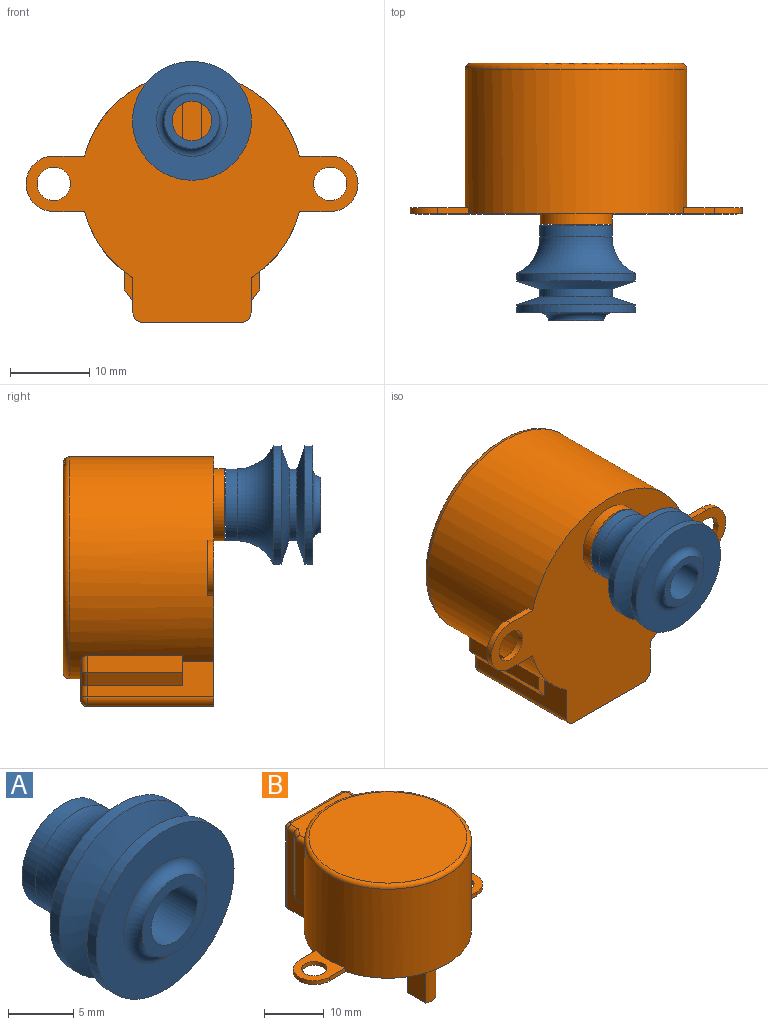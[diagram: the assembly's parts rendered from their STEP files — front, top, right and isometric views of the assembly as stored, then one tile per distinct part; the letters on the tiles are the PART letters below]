
ASSEMBLY  parts=2 mates=1
PART A: 12 faces, bbox 20.7x14.8x20.7 mm
  f0: cylinder r=7.5mm len=15mm, axis (0,-1,0), area 47.1mm2, adj f1,f10
  f1: cone r=4.55mm half-angle=71.3deg, axis (0,1,0), area 117.9mm2, adj f0,f2
  f2: cylinder r=4.55mm len=9.1mm, axis (0,-1,0), area 28.6mm2, adj f1,f3
  f3: cone r=4.55mm half-angle=71.3deg, axis (0,-1,0), area 117.9mm2, adj f2,f4
  f4: cylinder r=7.5mm len=15mm, axis (0,-1,0), area 47.1mm2, adj f3,f5
  f5: plane 15x15mm, normal (0,-1,0), area 113.2mm2, adj f4,f11
  f6: plane 6.99x6.99mm, normal (0,-1,0), area 18.8mm2, adj f7,f11
  f7: cylinder r=2.5mm len=12mm, axis (0,-1,0), area 188.3mm2, adj f6,f8
  f8: plane 9.1x9.1mm, normal (0,1,0), area 45.5mm2, adj f7,f9
  f9: cylinder r=4.55mm len=9.1mm, axis (0,-1,0), area 41.2mm2, adj f8,f10
  f10: torus R=9.55mm, axis (0,-1,0), area 201.3mm2, adj f0,f9
  f11: torus R=4.5mm, axis (0,1,0), area 38.1mm2, adj f5,f6
PART B: 43 faces, bbox 41.9x32.7x28.3 mm
  f0: plane 4.33x1.25mm, normal (0,0,-1), area 3.8mm2, adj f1,f4
  f1: cylinder r=2.5mm len=8mm, axis (0,0,1), area 62.8mm2, adj f0,f2,f3,f4,f5,f42
  f2: plane 4.33x1.25mm, normal (0,0,-1), area 3.8mm2, adj f1,f3
  f3: plane 6x4.33mm, normal (1,0,0), area 26mm2, adj f1,f2,f5
  f4: plane 6x4.33mm, normal (-1,0,0), area 26mm2, adj f0,f1,f5
  f5: plane 5x2.5mm, normal (0,0,-1), area 12mm2, adj f1,f3,f4
  f6: plane 16x4.45mm, normal (1,0,0), area 34.6mm2, adj f10,f12,f14,f15,f27,f28
  f7: plane 16x12.5mm, normal (0,1,0), area 200mm2, adj f10,f11,f12,f25
  f8: plane 16x4.45mm, normal (-1,0,0), area 34.6mm2, adj f10,f11,f16,f18,f23,f28
  f9: plane 15.54x5.05mm, normal (0,0,1), area 47.2mm2, adj f19,f20,f21,f22,f23,f24,f25,f26
  f10: plane 41.9x31.5mm, normal (0,0,-1), area 673.7mm2, adj f6,f7,f8,f11,f12,f28,f31,f32
  f11: cylinder r=1.2mm len=16mm, axis (0,0,-1), area 30.2mm2, adj f7,f8,f10,f24
  f12: cylinder r=1.2mm len=16mm, axis (0,0,-1), area 30.2mm2, adj f6,f7,f10,f26
  f13: plane 12x2.2mm, normal (1,0,0), area 26.4mm2, adj f14,f15,f20,f28
  f14: plane 12x1.63mm, normal (0.82,0.57,0), area 23.7mm2, adj f6,f13,f15,f19
  f15: plane 3.83x1.12mm, normal (0,0,-1), area 2.9mm2, adj f6,f13,f14,f28
  f16: plane 12x1.63mm, normal (-0.82,0.57,0), area 23.7mm2, adj f8,f17,f18,f22
  f17: plane 12x2.2mm, normal (-1,0,0), area 26.4mm2, adj f16,f18,f21,f28
  f18: plane 3.83x1.12mm, normal (0,0,-1), area 2.9mm2, adj f8,f16,f17,f28
  f19: cylinder r=0.8mm len=2.29mm, axis (0.57,-0.82,0), area 2.5mm2, adj f9,f14,f20,f27
  f20: cylinder r=0.8mm len=2.2mm, axis (0,-1,0), area 2.4mm2, adj f9,f13,f19,f28
  f21: cylinder r=0.8mm len=2.2mm, axis (0,1,0), area 2.4mm2, adj f9,f17,f22,f28
  f22: cylinder r=0.8mm len=2.29mm, axis (0.57,0.82,0), area 2.5mm2, adj f9,f16,f21,f23
  f23: cylinder r=0.8mm len=1.65mm, axis (0,-1,0), area 1.9mm2, adj f8,f9,f22,f24
  f24: torus R=0.4mm, axis (0,0,-1), area 1.8mm2, adj f9,f11,f23,f25
  f25: cylinder r=0.8mm len=12.5mm, axis (-1,0,0), area 15.7mm2, adj f7,f9,f24,f26
  f26: torus R=0.4mm, axis (0,0,-1), area 1.8mm2, adj f9,f12,f25,f27
  f27: cylinder r=0.8mm len=1.65mm, axis (0,1,0), area 1.9mm2, adj f6,f9,f19,f26
  f28: cylinder r=14mm len=28mm, axis (0,0,1), area 1295.5mm2, adj f6,f8,f9,f10,f13,f15,f17,f18
  f29: plane 26.5x26.5mm, normal (0,0,1), area 551.5mm2, adj f30
  f30: torus R=13.25mm, axis (0,0,-1), area 101.6mm2, adj f28,f29
  f31: cylinder r=3.5mm len=7mm, axis (0,0,-1), area 8.8mm2, adj f10,f32,f33,f34
  f32: plane 3.89x0.8mm, normal (0,1,0), area 3.1mm2, adj f10,f28,f31,f34
  f33: plane 3.89x0.8mm, normal (0,-1,0), area 3.1mm2, adj f10,f28,f31,f34
  f34: plane 7.39x7mm, normal (0,0,1), area 30.6mm2, adj f28,f31,f32,f33,f35
  f35: cylinder r=2.1mm len=4.2mm, axis (0,0,-1), area 10.6mm2, adj f10,f34
  f36: plane 3.89x0.8mm, normal (0,1,0), area 3.1mm2, adj f10,f28,f37,f39
  f37: cylinder r=3.5mm len=7mm, axis (0,0,-1), area 8.8mm2, adj f10,f36,f38,f39
  f38: plane 3.89x0.8mm, normal (0,-1,0), area 3.1mm2, adj f10,f28,f37,f39
  f39: plane 7.39x7mm, normal (0,0,1), area 30.6mm2, adj f28,f36,f37,f38,f40
  f40: cylinder r=2.1mm len=4.2mm, axis (0,0,-1), area 10.6mm2, adj f10,f39
  f41: cylinder r=4.55mm len=9.1mm, axis (0,0,1), area 37.2mm2, adj f10,f42
  f42: plane 9.1x9.1mm, normal (0,0,-1), area 45.4mm2, adj f1,f41
PLACE A t=(23.52,7.83,-10.01)mm
PLACE B rot(axis=(-1,0,0),90deg) t=(23.52,-6.71,-17.96)mm
MATE cylindrical A.f0 <-> B.f1  axis (0,-1,0) through (23.52,-27.19,-10.01)mm
